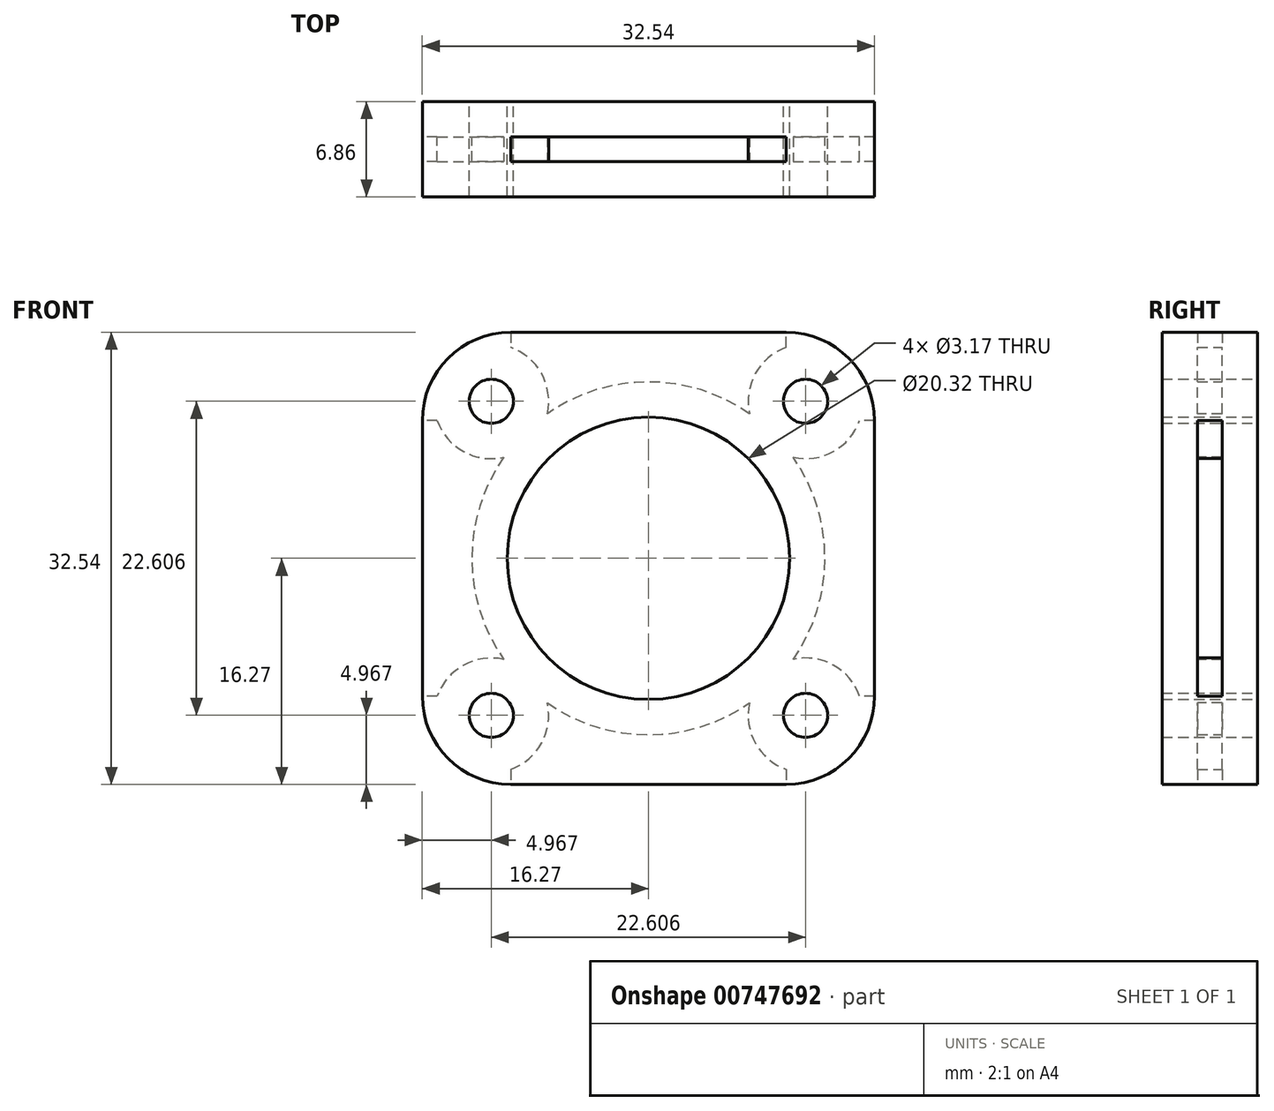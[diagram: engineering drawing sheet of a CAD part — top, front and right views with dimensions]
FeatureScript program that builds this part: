
annotation { "Feature Type Name" : "Feature", "Feature Type Description" : "" }
export const myFeature = defineFeature(function(context is Context, id is Id, definition is map)
    precondition{}
    {
        {
            var Q0;
            Q0=qCreatedBy(makeId("Front.planeOp"),FACE);
            var sketch = newSketch(context, id + "F0", { "sketchPlane" : qUnion([Q0])});
            skLineSegment(sketch, "E0.bottom", {"start": v(-9.92, 16.27) * mm, "end": v(9.92, 16.27) * mm});
            skLineSegment(sketch, "E0.top", {"start": v(-9.92, -16.27) * mm, "end": v(9.92, -16.27) * mm});
            skLineSegment(sketch, "E0.left", {"start": v(-16.27, 9.92) * mm, "end": v(-16.27, -9.92) * mm});
            skLineSegment(sketch, "E0.right", {"start": v(16.27, 9.92) * mm, "end": v(16.27, -9.92) * mm});
            skPoint(sketch, "E0.middle", {"position": v(0, 0) * mm});
            skCircle(sketch, "E1", {"center": v(0, 0) * mm, "radius": 10.16 * mm});
            skCircle(sketch, "E2", {"center": v(-11.3, 11.3) * mm, "radius": 1.59 * mm});
            skCircle(sketch, "E3", {"center": v(11.3, 11.3) * mm, "radius": 1.59 * mm});
            skCircle(sketch, "E4", {"center": v(-11.3, -11.3) * mm, "radius": 1.59 * mm});
            skCircle(sketch, "E5", {"center": v(11.3, -11.3) * mm, "radius": 1.59 * mm});
            skPoint(sketch, "E6.visualSharp", {"position": v(-16.27, 16.27) * mm});
            skArc(sketch, "E6.filletArc", {"start": v(-9.92, 16.27) * mm, "mid": v(-14.4, 14.4) * mm, "end": v(-16.27, 9.92) * mm});
            skPoint(sketch, "E7.visualSharp", {"position": v(16.27, 16.27) * mm});
            skArc(sketch, "E7.filletArc", {"start": v(16.27, 9.92) * mm, "mid": v(14.4, 14.4) * mm, "end": v(9.92, 16.27) * mm});
            skPoint(sketch, "E8.visualSharp", {"position": v(16.27, -16.27) * mm});
            skArc(sketch, "E8.filletArc", {"start": v(9.92, -16.27) * mm, "mid": v(14.4, -14.4) * mm, "end": v(16.27, -9.92) * mm});
            skPoint(sketch, "E9.visualSharp", {"position": v(-16.27, -16.27) * mm});
            skArc(sketch, "E9.filletArc", {"start": v(-16.27, -9.92) * mm, "mid": v(-14.4, -14.4) * mm, "end": v(-9.92, -16.27) * mm});
            skSolve(sketch);
        }
        {
            var Q0;
            Q0=makeQuery(id+"F0.imprint","IMPRINT",FACE,{"disambiguationData":[TD([[makeQuery(id+"F0.imprint","IMPRINT",EDGE,{"derivedFrom":sQuery(id+"F0.wireOp",EDGE,"E0.bottom")}),-1.0]])]});
            extrude(context, id + "F1", {"entities" : qUnion([Q0]), "depth" : 6.86 * mm, "offsetDistance" : 25.4 * mm});
        }
        {
            var Q0;
            Q0=makeQuery(id+"F1.opExtrude","SWEPT_FACE",FACE,{"disambiguationData":[OSD([sQuery(id+"F0.wireOp",EDGE,"E0.right")])]});
            var Q1;
            Q1=makeQuery(id+"F1.opExtrude","SWEPT_FACE",FACE,{"disambiguationData":[OSD([sQuery(id+"F0.wireOp",EDGE,"E0.bottom")])]});
            var Q2;
            Q2=makeQuery(id+"F1.opExtrude","SWEPT_FACE",FACE,{"disambiguationData":[OSD([sQuery(id+"F0.wireOp",EDGE,"E0.top")])]});
            var Q3;
            Q3=makeQuery(id+"F1.opExtrude","SWEPT_FACE",FACE,{"disambiguationData":[OSD([sQuery(id+"F0.wireOp",EDGE,"E0.left")])]});
            shell(context, id + "F2", {"entities" : qUnion([Q0, Q1, Q2, Q3]), "thickness" : 2.54 * mm});
        }
    });
